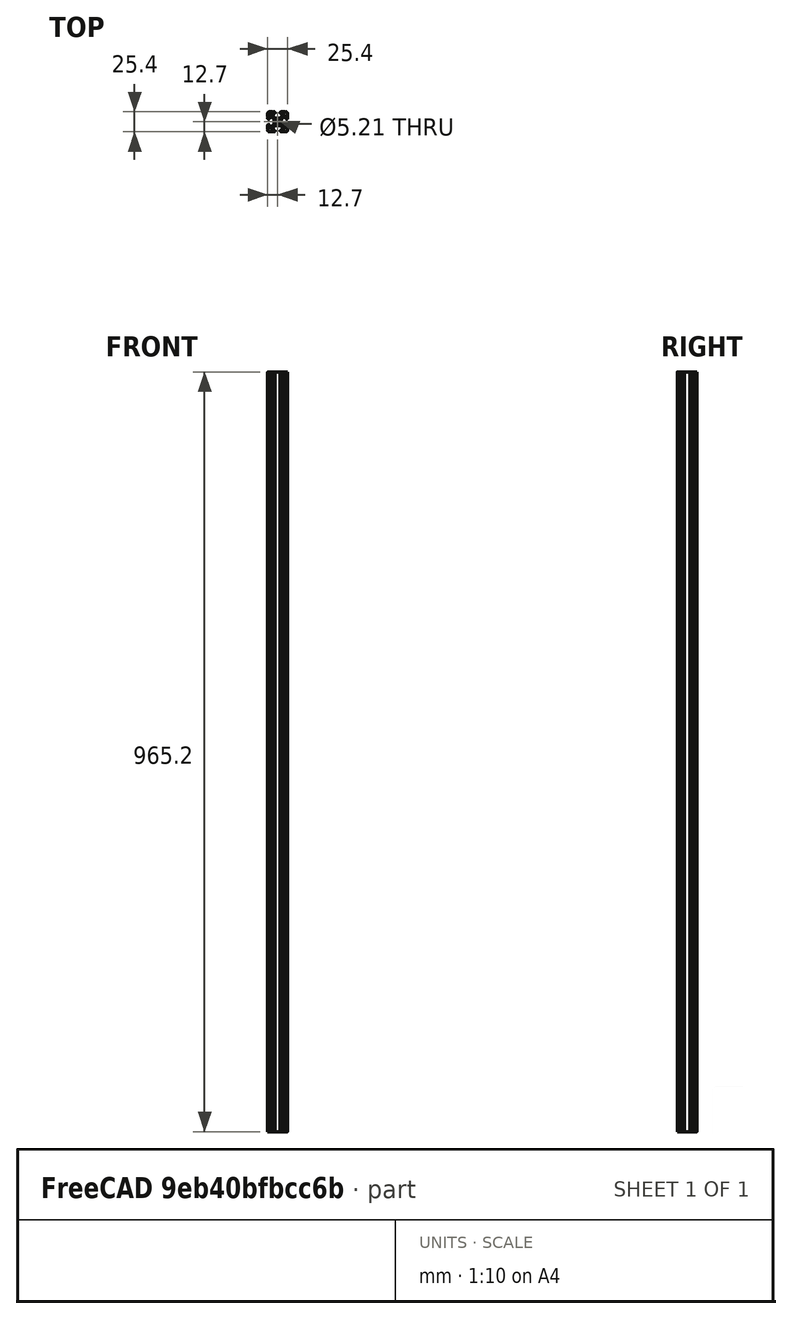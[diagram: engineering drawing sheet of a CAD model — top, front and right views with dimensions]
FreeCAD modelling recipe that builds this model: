
FCSTD DOCUMENT  (FreeCAD 0.18R4 (GitTag))
Label: 1010-38
License: All rights reserved
LicenseURL: http://en.wikipedia.org/wiki/All_rights_reserved
objects: Sketcher::SketchObject×1, Part::Extrusion×1
note: 2 computed .brp shape members not serialized (recipe doc carries the construction recipe); baked Part::Feature solids carry a one-line shape summary decoded from their .brp

FEATURE [Sketcher::SketchObject] Sketch097
  sketch-geometry (97):
    g0: Circle CenterX=0 CenterY=0 CenterZ=0 NormalX=0 NormalY=0 NormalZ=-1 AngleXU=0 Radius=2.6035
    g1: ArcOfCircle CenterX=12.7 CenterY=5.82508 CenterZ=0 NormalX=0 NormalY=0 NormalZ=1 AngleXU=0 Radius=0.508 StartAngle=1.5708 EndAngle=4.71239
    g2: LineSegment StartX=3.2385 StartY=11.651 StartZ=0 EndX=3.2385 EndY=11.5392 EndZ=0
    g3: LineSegment StartX=6.33313 StartY=-12.7 StartZ=0 EndX=9.55044 EndY=-12.7 EndZ=0
    g4: LineSegment StartX=7.20704 StartY=8.72437 StartZ=0 EndX=3.89827 EndY=5.42317 EndZ=0
    g5: ArcOfCircle CenterX=7.6835 CenterY=1.59319 CenterZ=0 NormalX=0 NormalY=0 NormalZ=1 AngleXU=0 Radius=3.175 StartAngle=2.35505 EndAngle=3.14159
    g6: ArcOfCircle CenterX=-1.70925 CenterY=-7.6708 CenterZ=0 NormalX=0 NormalY=0 NormalZ=1 AngleXU=0 Radius=3.175 StartAngle=1.5708 EndAngle=2.35528
    g7: ArcOfCircle CenterX=11.5392 CenterY=-4.28747 CenterZ=0 NormalX=0 NormalY=0 NormalZ=1 AngleXU=0 Radius=1.04901 StartAngle=1.5708 EndAngle=3.14159
    g8: ArcOfCircle CenterX=12.7 CenterY=-5.82508 CenterZ=0 NormalX=0 NormalY=0 NormalZ=1 AngleXU=0 Radius=0.508 StartAngle=1.5708 EndAngle=4.71239
    g9: LineSegment StartX=4.28751 StartY=10.4902 StartZ=0 EndX=6.47679 EndY=10.4902 EndZ=0
    g10: ArcOfCircle CenterX=4.28751 CenterY=11.651 CenterZ=0 NormalX=0 NormalY=0 NormalZ=1 AngleXU=0 Radius=1.04901 StartAngle=1.5708 EndAngle=3.14159
    g11: ArcOfCircle CenterX=6.47679 CenterY=9.45629 CenterZ=0 NormalX=0 NormalY=0 NormalZ=1 AngleXU=0 Radius=1.03391 StartAngle=5.49664 EndAngle=7.85398
    g12: ArcOfCircle CenterX=4.28751 CenterY=11.5392 CenterZ=0 NormalX=0 NormalY=0 NormalZ=1 AngleXU=0 Radius=1.04901 StartAngle=3.14159 EndAngle=4.71239
    g13: LineSegment StartX=3.95227 StartY=-5.42369 StartZ=0 EndX=7.17965 EndY=-8.64519 EndZ=0
    g14: ArcOfCircle CenterX=11.651 CenterY=4.28747 CenterZ=0 NormalX=0 NormalY=0 NormalZ=1 AngleXU=0 Radius=1.04901 StartAngle=4.71239 EndAngle=6.28319
    g15: ArcOfCircle CenterX=-5.82513 CenterY=-12.7 CenterZ=0 NormalX=0 NormalY=0 NormalZ=1 AngleXU=0 Radius=0.508 StartAngle=0 EndAngle=3.14159
    g16: LineSegment StartX=-6.47679 StartY=10.4902 StartZ=0 EndX=-4.28751 EndY=10.4902 EndZ=0
    g17: ArcOfCircle CenterX=-12.7 CenterY=10.0584 CenterZ=0 NormalX=0 NormalY=0 NormalZ=1 AngleXU=0 Radius=0.508 StartAngle=4.71239 EndAngle=7.85368
    g18: ArcOfCircle CenterX=-12.7 CenterY=5.82508 CenterZ=0 NormalX=0 NormalY=0 NormalZ=1 AngleXU=0 Radius=0.508 StartAngle=4.71239 EndAngle=7.85398
    g19: LineSegment StartX=-11.5392 StartY=-3.23846 StartZ=0 EndX=-11.651 EndY=-3.23846 EndZ=0
    g20: LineSegment StartX=-3.89827 StartY=5.42317 StartZ=0 EndX=-7.20704 EndY=8.72437 EndZ=0
    g21: LineSegment StartX=1.65578 StartY=4.4958 StartZ=0 EndX=-1.65578 EndY=4.4958 EndZ=0
    g22: ArcOfCircle CenterX=-1.65578 CenterY=7.6708 CenterZ=0 NormalX=0 NormalY=0 NormalZ=1 AngleXU=0 Radius=3.175 StartAngle=3.92813 EndAngle=4.71239
    g23: LineSegment StartX=-9.55044 StartY=-12.7 StartZ=0 EndX=-6.33313 EndY=-12.7 EndZ=0
    g24: ArcOfCircle CenterX=-5.82513 CenterY=12.7 CenterZ=0 NormalX=0 NormalY=0 NormalZ=1 AngleXU=0 Radius=0.508 StartAngle=3.14159 EndAngle=6.28319
    g25: ArcOfCircle CenterX=-4.28751 CenterY=11.651 CenterZ=0 NormalX=0 NormalY=0 NormalZ=1 AngleXU=0 Radius=1.04901 StartAngle=0 EndAngle=1.5708
    g26: LineSegment StartX=-12.7 StartY=-4.28747 StartZ=0 EndX=-12.7 EndY=-5.31708 EndZ=0
    g27: ArcOfCircle CenterX=-6.47679 CenterY=9.45629 CenterZ=0 NormalX=0 NormalY=0 NormalZ=1 AngleXU=0 Radius=1.03391 StartAngle=1.5708 EndAngle=3.92813
    g28: ArcOfCircle CenterX=-4.28751 CenterY=11.5392 CenterZ=0 NormalX=0 NormalY=0 NormalZ=1 AngleXU=0 Radius=1.04901 StartAngle=4.71239 EndAngle=6.28319
    g29: LineSegment StartX=-5.44101 StartY=-3.84082 StartZ=0 EndX=-8.73713 EndY=-7.12941 EndZ=0
    g30: ArcOfCircle CenterX=-7.6835 CenterY=-1.59319 CenterZ=0 NormalX=0 NormalY=0 NormalZ=1 AngleXU=0 Radius=3.175 StartAngle=5.49664 EndAngle=6.28319
    g31: LineSegment StartX=-12.7 StartY=5.31708 StartZ=0 EndX=-12.7 EndY=4.28747 EndZ=0
    g32: LineSegment StartX=-8.73713 StartY=7.12941 StartZ=0 EndX=-5.44101 EndY=3.84082 EndZ=0
    g33: LineSegment StartX=-11.651 StartY=3.23846 StartZ=0 EndX=-11.5392 EndY=3.23846 EndZ=0
    g34: ArcOfCircle CenterX=-9.46279 CenterY=-6.40209 CenterZ=0 NormalX=0 NormalY=0 NormalZ=1 AngleXU=0 Radius=1.02741 StartAngle=3.14159 EndAngle=5.49664
    g35: ArcOfCircle CenterX=-10.5918 CenterY=10.5918 CenterZ=0 NormalX=0 NormalY=0 NormalZ=1 AngleXU=0 Radius=2.1082 StartAngle=1.55877 EndAngle=3.15364
    g36: LineSegment StartX=-12.7 StartY=9.5504 StartZ=0 EndX=-12.7 EndY=6.33308 EndZ=0
    g37: LineSegment StartX=-6.33313 StartY=12.7 StartZ=0 EndX=-9.55044 EndY=12.7 EndZ=0
    g38: ArcOfCircle CenterX=-11.5392 CenterY=-4.28747 CenterZ=0 NormalX=0 NormalY=0 NormalZ=1 AngleXU=0 Radius=1.04901 StartAngle=0 EndAngle=1.5708
    g39: LineSegment StartX=4.28751 StartY=-12.7 StartZ=0 EndX=5.31713 EndY=-12.7 EndZ=0
    g40: LineSegment StartX=5.44101 StartY=3.84082 StartZ=0 EndX=8.73713 EndY=7.12941 EndZ=0
    g41: LineSegment StartX=10.4902 StartY=-4.28747 StartZ=0 EndX=10.4902 EndY=-6.40209 EndZ=0
    g42: ArcOfCircle CenterX=9.46279 CenterY=6.40209 CenterZ=0 NormalX=0 NormalY=0 NormalZ=1 AngleXU=0 Radius=1.02741 StartAngle=0 EndAngle=2.35505
    g43: ArcOfCircle CenterX=5.82513 CenterY=-12.7 CenterZ=0 NormalX=0 NormalY=0 NormalZ=1 AngleXU=0 Radius=0.508 StartAngle=0 EndAngle=3.14159
    g44: LineSegment StartX=12.7 StartY=-9.5504 StartZ=0 EndX=12.7 EndY=-6.33308 EndZ=0
    g45: LineSegment StartX=4.5085 StartY=-1.59319 StartZ=0 EndX=4.5085 EndY=1.59319 EndZ=0
    g46: ArcOfCircle CenterX=12.7 CenterY=10.0584 CenterZ=0 NormalX=0 NormalY=0 NormalZ=1 AngleXU=0 Radius=0.508 StartAngle=1.5711 EndAngle=4.71239
    g47: ArcOfCircle CenterX=12.7 CenterY=-10.0584 CenterZ=0 NormalX=0 NormalY=0 NormalZ=1 AngleXU=0 Radius=0.508 StartAngle=1.5708 EndAngle=4.71209
    g48: LineSegment StartX=3.2385 StartY=-11.5392 StartZ=0 EndX=3.2385 EndY=-11.651 EndZ=0
    g49: LineSegment StartX=8.73713 StartY=-7.12941 StartZ=0 EndX=5.44101 EndY=-3.84082 EndZ=0
    g50: ArcOfCircle CenterX=11.651 CenterY=-4.28747 CenterZ=0 NormalX=0 NormalY=0 NormalZ=1 AngleXU=0 Radius=1.04901 StartAngle=0 EndAngle=1.5708
    g51: ArcOfCircle CenterX=1.65578 CenterY=7.6708 CenterZ=0 NormalX=0 NormalY=0 NormalZ=1 AngleXU=0 Radius=3.175 StartAngle=4.71239 EndAngle=5.49664
    g52: ArcOfCircle CenterX=7.6835 CenterY=-1.59319 CenterZ=0 NormalX=0 NormalY=0 NormalZ=1 AngleXU=0 Radius=3.175 StartAngle=3.14159 EndAngle=3.92813
    g53: LineSegment StartX=12.7 StartY=4.28747 StartZ=0 EndX=12.7 EndY=5.31708 EndZ=0
    g54: ArcOfCircle CenterX=6.41641 CenterY=-9.40983 CenterZ=0 NormalX=0 NormalY=0 NormalZ=1 AngleXU=0 Radius=1.08037 StartAngle=4.71239 EndAngle=7.06949
    g55: LineSegment StartX=12.7 StartY=-5.31708 StartZ=0 EndX=12.7 EndY=-4.28747 EndZ=0
    g56: ArcOfCircle CenterX=10.0584 CenterY=-12.7 CenterZ=0 NormalX=0 NormalY=0 NormalZ=1 AngleXU=0 Radius=0.508 StartAngle=0.000300194 EndAngle=3.14159
    g57: ArcOfCircle CenterX=11.5392 CenterY=4.28747 CenterZ=0 NormalX=0 NormalY=0 NormalZ=1 AngleXU=0 Radius=1.04901 StartAngle=3.14159 EndAngle=4.71239
    g58: LineSegment StartX=12.7 StartY=6.33308 StartZ=0 EndX=12.7 EndY=9.5504 EndZ=0
    g59: ArcOfCircle CenterX=4.28751 CenterY=-11.5392 CenterZ=0 NormalX=0 NormalY=0 NormalZ=1 AngleXU=0 Radius=1.04901 StartAngle=1.5708 EndAngle=3.14159
    g60: ArcOfCircle CenterX=10.5918 CenterY=10.5918 CenterZ=0 NormalX=0 NormalY=0 NormalZ=1 AngleXU=0 Radius=2.1082 StartAngle=6.27114 EndAngle=7.86601
    g61: ArcOfCircle CenterX=9.46279 CenterY=-6.40209 CenterZ=0 NormalX=0 NormalY=0 NormalZ=1 AngleXU=0 Radius=1.02741 StartAngle=3.92813 EndAngle=6.28319
    g62: LineSegment StartX=6.41641 StartY=-10.4902 StartZ=0 EndX=4.28751 EndY=-10.4902 EndZ=0
    g63: LineSegment StartX=-10.4902 StartY=-6.40209 StartZ=0 EndX=-10.4902 EndY=-4.28747 EndZ=0
    g64: ArcOfCircle CenterX=-9.46279 CenterY=6.40209 CenterZ=0 NormalX=0 NormalY=0 NormalZ=1 AngleXU=0 Radius=1.02741 StartAngle=0.786542 EndAngle=3.14159
    g65: LineSegment StartX=-10.4902 StartY=4.28747 StartZ=0 EndX=-10.4902 EndY=6.40209 EndZ=0
    g66: LineSegment StartX=-4.5085 StartY=1.59319 StartZ=0 EndX=-4.5085 EndY=-1.59319 EndZ=0
    g67: LineSegment StartX=-4.28751 StartY=12.7 StartZ=0 EndX=-5.31713 EndY=12.7 EndZ=0
    g68: ArcOfCircle CenterX=-11.5392 CenterY=4.28747 CenterZ=0 NormalX=0 NormalY=0 NormalZ=1 AngleXU=0 Radius=1.04901 StartAngle=4.71239 EndAngle=6.28319
    g69: LineSegment StartX=-3.2385 StartY=11.5392 StartZ=0 EndX=-3.2385 EndY=11.651 EndZ=0
    g70: ArcOfCircle CenterX=-11.651 CenterY=4.28747 CenterZ=0 NormalX=0 NormalY=0 NormalZ=1 AngleXU=0 Radius=1.04901 StartAngle=3.14159 EndAngle=4.71239
    g71: ArcOfCircle CenterX=-7.6835 CenterY=1.59319 CenterZ=0 NormalX=0 NormalY=0 NormalZ=1 AngleXU=0 Radius=3.175 StartAngle=0 EndAngle=0.786542
    g72: ArcOfCircle CenterX=-10.0584 CenterY=12.7 CenterZ=0 NormalX=0 NormalY=0 NormalZ=1 AngleXU=0 Radius=0.508 StartAngle=3.14189 EndAngle=6.28319
    g73: LineSegment StartX=-1.70925 StartY=-4.4958 StartZ=0 EndX=1.70925 EndY=-4.4958 EndZ=0
    g74: LineSegment StartX=11.651 StartY=-3.23846 StartZ=0 EndX=11.5392 EndY=-3.23846 EndZ=0
    g75: ArcOfCircle CenterX=-10.5918 CenterY=-10.5918 CenterZ=0 NormalX=0 NormalY=0 NormalZ=1 AngleXU=0 Radius=2.1082 StartAngle=3.12954 EndAngle=4.72442
    g76: ArcOfCircle CenterX=10.5918 CenterY=-10.5918 CenterZ=0 NormalX=0 NormalY=0 NormalZ=1 AngleXU=0 Radius=2.1082 StartAngle=4.70036 EndAngle=6.29523
    g77: ArcOfCircle CenterX=-12.7 CenterY=-5.82508 CenterZ=0 NormalX=0 NormalY=0 NormalZ=1 AngleXU=0 Radius=0.508 StartAngle=4.71239 EndAngle=7.85398
    g78: ArcOfCircle CenterX=5.82513 CenterY=12.7 CenterZ=0 NormalX=0 NormalY=0 NormalZ=1 AngleXU=0 Radius=0.508 StartAngle=3.14159 EndAngle=6.28319
    g79: LineSegment StartX=9.55044 StartY=12.7 StartZ=0 EndX=6.33313 EndY=12.7 EndZ=0
    g80: ArcOfCircle CenterX=10.0584 CenterY=12.7 CenterZ=0 NormalX=0 NormalY=0 NormalZ=1 AngleXU=0 Radius=0.508 StartAngle=3.14159 EndAngle=6.28289
    g81: ArcOfCircle CenterX=1.70925 CenterY=-7.6708 CenterZ=0 NormalX=0 NormalY=0 NormalZ=1 AngleXU=0 Radius=3.175 StartAngle=0.78631 EndAngle=1.5708
    g82: ArcOfCircle CenterX=4.28751 CenterY=-11.651 CenterZ=0 NormalX=0 NormalY=0 NormalZ=1 AngleXU=0 Radius=1.04901 StartAngle=3.14159 EndAngle=4.71239
    g83: LineSegment StartX=5.31713 StartY=12.7 StartZ=0 EndX=4.28751 EndY=12.7 EndZ=0
    g84: LineSegment StartX=10.4902 StartY=6.40209 StartZ=0 EndX=10.4902 EndY=4.28747 EndZ=0
    g85: LineSegment StartX=11.5392 StartY=3.23846 StartZ=0 EndX=11.651 EndY=3.23846 EndZ=0
    g86: ArcOfCircle CenterX=-10.0584 CenterY=-12.7 CenterZ=0 NormalX=0 NormalY=0 NormalZ=1 AngleXU=0 Radius=0.508 StartAngle=0 EndAngle=3.14129
    g87: ArcOfCircle CenterX=-12.7 CenterY=-10.0584 CenterZ=0 NormalX=0 NormalY=0 NormalZ=1 AngleXU=0 Radius=0.508 StartAngle=4.71269 EndAngle=7.85398
    g88: ArcOfCircle CenterX=-4.28751 CenterY=-11.5392 CenterZ=0 NormalX=0 NormalY=0 NormalZ=1 AngleXU=0 Radius=1.04901 StartAngle=0 EndAngle=1.5708
    g89: ArcOfCircle CenterX=-4.28751 CenterY=-11.651 CenterZ=0 NormalX=0 NormalY=0 NormalZ=1 AngleXU=0 Radius=1.04901 StartAngle=4.71239 EndAngle=6.28319
    g90: LineSegment StartX=-12.7 StartY=-6.33308 StartZ=0 EndX=-12.7 EndY=-9.5504 EndZ=0
    g91: ArcOfCircle CenterX=-11.651 CenterY=-4.28747 CenterZ=0 NormalX=0 NormalY=0 NormalZ=1 AngleXU=0 Radius=1.04901 StartAngle=1.5708 EndAngle=3.14159
    g92: LineSegment StartX=-7.17965 StartY=-8.64519 StartZ=0 EndX=-3.95227 EndY=-5.42369 EndZ=0
    g93: LineSegment StartX=-5.31713 StartY=-12.7 StartZ=0 EndX=-4.28751 EndY=-12.7 EndZ=0
    g94: LineSegment StartX=-3.2385 StartY=-11.651 StartZ=0 EndX=-3.2385 EndY=-11.5392 EndZ=0
    g95: ArcOfCircle CenterX=-6.41641 CenterY=-9.40983 CenterZ=0 NormalX=0 NormalY=0 NormalZ=1 AngleXU=0 Radius=1.08037 StartAngle=2.35528 EndAngle=4.71239
    g96: LineSegment StartX=-4.28751 StartY=-10.4902 StartZ=0 EndX=-6.41641 EndY=-10.4902 EndZ=0
FEATURE [Part::Extrusion] Extrude
  Base = -> Sketch097
  Dir = (0,0,1)
  DirMode = 2
  FaceMakerClass = Part::FaceMakerBullseye
  LengthFwd = 965.2
  LengthRev = 0
  Solid = true
  Symmetric = false
